# Revit family: City Class F
name_source: partatom
category: Attrezzatura meccanica
units: mm (PartAtom-declared; Revit-internal decimal feet)

## family parameters
Basato su piano di lavoro = No
Classificazione = Nessuno
Condiviso = No
Mantieni orientamento annotazione = No
Punto di calcolo locali = No
Quota connettore circolare = Usa diametro
Sempre verticale = Sì
Taglio con vuoti quando caricato = No
Tipo di parte = Normale

## types (8) — shared parameters
Date of publishing = 05/02/2024
Depth = 324 mm  [stored 1.06299 ft]
Design country = Italy
Domestic Cold Water Diameter = 21 mm  [stored 0.0688976 ft]
Domestic Hot Water Diameter = 21 mm  [stored 0.0688976 ft]
Flue outlet = 80 mm  [stored 0.262467 ft]
Gas Inlet Diameter = 26 mm  [stored 0.0853018 ft]
Height = 700 mm  [stored 2.29659 ft]
Hydronic Return Diameter = 26 mm  [stored 0.0853018 ft]
Hydronic Supply Diameter = 26 mm  [stored 0.0853018 ft]
IFC Classification = Boilers
Manufacturer country = Italy
Manufacturer name = Italtherm S.p.A.
Material main = Metal
Material secondary = Plastic
Max supply pressure = 6 bar
Max system temperature = 85°C
Max working pressure = 3 bar
NBS reference Description = Boilers
Power supply | Frequency (Hz) = 50 Hz
Power supply | Phase = 1
Power supply | Voltage (V) = 230 V
Product family = Heating
Product group = Thermal unit
Uniclass 2015 Name = Boilers
Width = 400 mm  [stored 1.31234 ft]
zero-valued in all types: Prospetto di default

## per-type parameters (varying)
| type | Efficiency 30% | Max heat input (Qn) | Max heat output (Pn) | Min heat input (Qr) | Min heat output (Pr) | Power consumption (W) | Weight |
| City Class 12 F | 91,00% | 25.7 kW | 24 kW | 10 kW | 8.5 kW | 103 W | 30,40 kg |
| City Class 16 F | 91,00% | 25.7 kW | 24 kW | 10 kW | 8,5 kW | 103 W | 30,40 kg |
| City Class 18 F | 91,00% | 25.7 kW | 24 kW | 10 kW | 8,5 kW | 103 W | 30,40 kg |
| City Class 20 F | 90,50% | 21 kW | 19.5 kW | 9.5 kW | 8.1 kW | 103 W | 30,40 kg |
| City Class 25 F | 91,00% | 25.7 kW | 24 kW | 10 kW | 8.5 kW | 103 W | 30,60 kg |
| City Class 30 F | 91,50% | 30 kW | 28.2 kW | 12 kW | 10.2 k W | 132 W | 31,60 kg |
| City Class 35 F | 92,00% | 34,5 kW | 32.4 kW | 13.6 kW | 11.7 kW | 145 W | 35,80 kg |
| City Class 40 F | 87,00% | 39,5 kW | 36.6 kW | 14 kW | 12 kW | 144 W | 36,50 kg |

note: [stored X ft] marks values corroborated as IEEE doubles in the binary element streams (Revit-internal decimal feet)
